annotation { "Feature Type Name" : "Feature", "Feature Type Description" : "" }
export const myFeature = defineFeature(function(context is Context, id is Id, definition is map)
    precondition{}
    {
        {
            var Q0;
            Q0=qCreatedBy(makeId("Top.planeOp"),FACE);
            var sketch = newSketch(context, id + "F0", { "sketchPlane" : qUnion([Q0])});
            skLineSegment(sketch, "E0.bottom", {"start": v(-292.1, 50.8) * mm, "end": v(292.1, 50.8) * mm});
            skLineSegment(sketch, "E0.top", {"start": v(-292.1, -50.8) * mm, "end": v(292.1, -50.8) * mm});
            skLineSegment(sketch, "E0.left", {"start": v(-292.1, 50.8) * mm, "end": v(-292.1, -50.8) * mm});
            skLineSegment(sketch, "E0.right", {"start": v(292.1, 50.8) * mm, "end": v(292.1, -50.8) * mm});
            skPoint(sketch, "E1", {"position": v(0, 50.8) * mm});
            skPoint(sketch, "E2", {"position": v(-292.1, 0) * mm});
            skText(sketch, "E3", { "text": "FITTINGS KIT", "fontName": "AllertaStencil-Regular.ttf"});
            skCircle(sketch, "E4", {"center": v(0, 44.45) * mm, "radius": 2.38 * mm});
            skCircle(sketch, "E5", {"center": v(12.7, 44.45) * mm, "radius": 2.38 * mm});
            skCircle(sketch, "E6", {"center": v(25.4, 44.45) * mm, "radius": 2.38 * mm});
            skCircle(sketch, "E7", {"center": v(-12.7, 44.45) * mm, "radius": 2.38 * mm});
            skCircle(sketch, "E8", {"center": v(-25.4, 44.45) * mm, "radius": 2.38 * mm});
            skCircle(sketch, "E9", {"center": v(279.4, 44.45) * mm, "radius": 2.38 * mm});
            skCircle(sketch, "E10", {"center": v(-279.4, 44.45) * mm, "radius": 2.38 * mm});
            skCircle(sketch, "E11", {"center": v(-266.7, 44.45) * mm, "radius": 2.38 * mm});
            skCircle(sketch, "E12", {"center": v(-254, 44.45) * mm, "radius": 2.38 * mm});
            skCircle(sketch, "E13", {"center": v(-241.3, 44.45) * mm, "radius": 2.38 * mm});
            skCircle(sketch, "E14", {"center": v(-228.6, 44.45) * mm, "radius": 2.38 * mm});
            skCircle(sketch, "E15", {"center": v(266.7, 44.45) * mm, "radius": 2.38 * mm});
            skCircle(sketch, "E16", {"center": v(254, 44.45) * mm, "radius": 2.38 * mm});
            skCircle(sketch, "E17", {"center": v(241.3, 44.45) * mm, "radius": 2.38 * mm});
            skCircle(sketch, "E18", {"center": v(228.6, 44.45) * mm, "radius": 2.38 * mm});
            const initialGuessF0  = {"E3": [-0.27698, -0.0381, 1, 0, 0.0635]};
            skSetInitialGuess(sketch, initialGuessF0);
            skSolve(sketch);
        }
        {
            var Q0;
            Q0 = qSketchRegion(id + "F0", true);
            extrude(context, id + "F1", {"entities" : qUnion([Q0]), "depth" : 6.35 * mm});
        }
    });